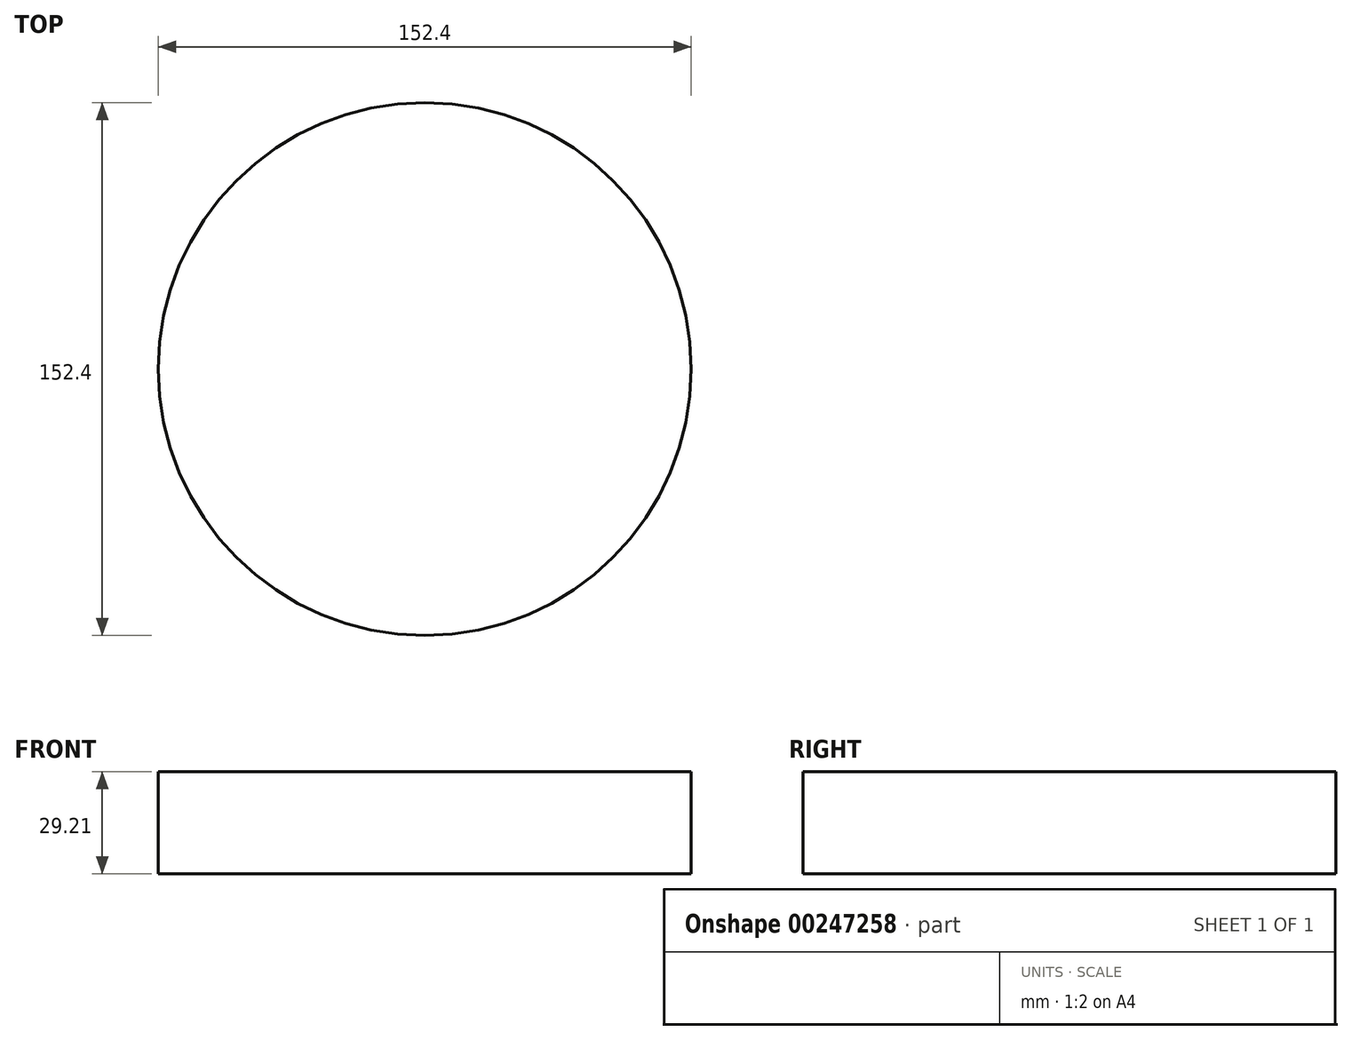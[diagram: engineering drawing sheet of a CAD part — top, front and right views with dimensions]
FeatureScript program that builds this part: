
annotation { "Feature Type Name" : "Feature", "Feature Type Description" : "" }
export const myFeature = defineFeature(function(context is Context, id is Id, definition is map)
    precondition{}
    {
        {
            var Q0;
            Q0=qCreatedBy(makeId("Top.planeOp"),FACE);
            var sketch = newSketch(context, id + "F0", { "sketchPlane" : qUnion([Q0])});
            skCircle(sketch, "E0", {"center": v(0, 0) * mm, "radius": 76.2 * mm});
            skSolve(sketch);
        }
        {
            var Q0;
            Q0=qSketchRegion(id+"F0",true);
            extrude(context, id + "F1", {"entities" : qUnion([Q0]), "depth" : 29.2 * mm});
        }
    });
